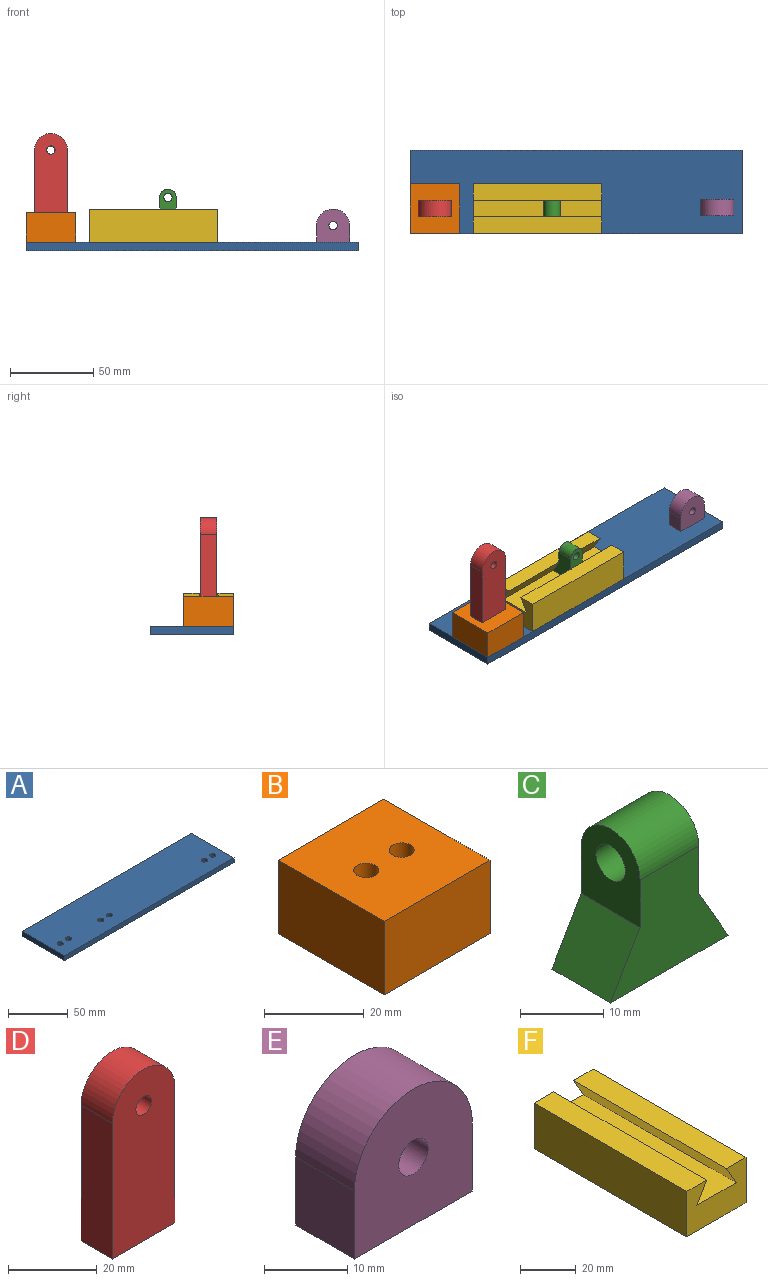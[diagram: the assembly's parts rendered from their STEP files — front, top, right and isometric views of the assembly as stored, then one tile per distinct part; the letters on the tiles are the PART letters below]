
ASSEMBLY  parts=6 mates=5
PART A: 12 faces, bbox 200x50x5 mm
  f0: plane 200x5mm, normal (0,1,0), area 1000mm2, adj f1,f9,f10,f11
  f1: plane 50x5mm, normal (-1,0,0), area 250mm2, adj f0,f2,f10,f11
  f2: plane 200x5mm, normal (0,-1,0), area 1000mm2, adj f1,f9,f10,f11
  f3: cylinder r=2.5mm len=5mm, axis (0,0,-1), area 78.5mm2, adj f10,f11
  f4: cylinder r=2.5mm len=5mm, axis (0,0,-1), area 78.5mm2, adj f10,f11
  f5: cylinder r=2.5mm len=5mm, axis (0,0,-1), area 78.5mm2, adj f10,f11
  f6: cylinder r=2.5mm len=5mm, axis (0,0,-1), area 78.5mm2, adj f10,f11
  f7: cylinder r=2.5mm len=5mm, axis (0,0,-1), area 78.5mm2, adj f10,f11
  f8: cylinder r=2.5mm len=5mm, axis (0,0,-1), area 78.5mm2, adj f10,f11
  f9: plane 50x5mm, normal (1,0,0), area 250mm2, adj f0,f2,f10,f11
  f10: plane 200x50mm, normal (0,0,1), area 9882.2mm2, adj f0,f1,f2,f3,f4,f5,f6,f7
  f11: plane 200x50mm, normal (0,0,-1), area 9882.2mm2, adj f0,f1,f2,f3,f4,f5,f6,f7
PART B: 8 faces, bbox 30x30x18 mm
  f0: plane 30x18mm, normal (0,1,0), area 540mm2, adj f1,f5,f6,f7
  f1: plane 30x18mm, normal (-1,0,0), area 540mm2, adj f0,f2,f6,f7
  f2: plane 30x18mm, normal (0,-1,0), area 540mm2, adj f1,f5,f6,f7
  f3: cylinder r=2.5mm len=18mm, axis (0,0,-1), area 282.7mm2, adj f6,f7
  f4: cylinder r=2.5mm len=18mm, axis (0,0,-1), area 282.7mm2, adj f6,f7
  f5: plane 30x18mm, normal (1,0,0), area 540mm2, adj f0,f2,f6,f7
  f6: plane 30x30mm, normal (0,0,1), area 860.7mm2, adj f0,f1,f2,f3,f4,f5
  f7: plane 30x30mm, normal (0,0,-1), area 860.7mm2, adj f0,f1,f2,f3,f4,f5
PART C: 9 faces, bbox 20x10x20.7 mm
  f0: plane 10x8.66mm, normal (-0.87,0,0.5), area 100mm2, adj f1,f3,f4,f5
  f1: plane 20x10mm, normal (0,0,-1), area 200mm2, adj f0,f2,f3,f4
  f2: plane 10x8.66mm, normal (0.87,0,0.5), area 100mm2, adj f1,f3,f4,f8
  f3: plane 20x15.66mm, normal (0,-1,0), area 199.9mm2, adj f0,f1,f2,f5,f6,f8
  f4: plane 20x15.66mm, normal (0,1,0), area 199.9mm2, adj f0,f1,f2,f5,f6,f8
  f5: plane 12x10mm, normal (-1,0,0), area 89.6mm2, adj f0,f3,f4,f6,f7
  f6: cylinder r=5mm len=10mm, axis (1,0,0), area 157.1mm2, adj f3,f4,f5,f8
  f7: cylinder r=2.5mm len=10mm, axis (1,0,0), area 157.1mm2, adj f5,f8
  f8: plane 12x10mm, normal (1,0,0), area 89.6mm2, adj f2,f3,f4,f6,f7
PART D: 11 faces, bbox 20x10x47.5 mm
  f0: plane 47.5x20mm, normal (0,1,0), area 887.4mm2, adj f1,f3,f4,f5,f6
  f1: plane 37.5x10mm, normal (-1,0,0), area 375mm2, adj f0,f2,f4,f5
  f2: plane 47.5x20mm, normal (0,-1,0), area 887.4mm2, adj f1,f3,f4,f5,f6
  f3: plane 37.5x10mm, normal (1,0,0), area 375mm2, adj f0,f2,f4,f5
  f4: plane 20x10mm, normal (0,0,-1), area 160.7mm2, adj f0,f1,f2,f3,f7,f9
  f5: cylinder r=10mm len=20mm, axis (0,-1,0), area 314.2mm2, adj f0,f1,f2,f3
  f6: cylinder r=2.5mm len=10mm, axis (0,-1,0), area 157.1mm2, adj f0,f2
  f7: cylinder r=2.5mm len=10mm, axis (0,0,-1), area 157.1mm2, adj f4,f8
  f8: plane 5x5mm, normal (0,0,-1), area 19.6mm2, adj f7
  f9: cylinder r=2.5mm len=10mm, axis (0,0,-1), area 157.1mm2, adj f4,f10
  f10: plane 5x5mm, normal (0,0,-1), area 19.6mm2, adj f9
PART E: 11 faces, bbox 20x10x20 mm
  f0: plane 10x10mm, normal (-1,0,0), area 100mm2, adj f1,f4,f5,f6
  f1: plane 20x10mm, normal (0,0,-1), area 160.7mm2, adj f0,f2,f5,f6,f7,f9
  f2: plane 10x10mm, normal (1,0,0), area 100mm2, adj f1,f4,f5,f6
  f3: cylinder r=2.5mm len=10mm, axis (0,1,0), area 157.1mm2, adj f5,f6
  f4: cylinder r=10mm len=20mm, axis (0,1,0), area 314.2mm2, adj f0,f2,f5,f6
  f5: plane 20x20mm, normal (0,-1,0), area 337.4mm2, adj f0,f1,f2,f3,f4
  f6: plane 20x20mm, normal (0,1,0), area 337.4mm2, adj f0,f1,f2,f3,f4
  f7: cylinder r=2.5mm len=5mm, axis (0,0,-1), area 78.5mm2, adj f1,f8
  f8: plane 5x5mm, normal (0,0,-1), area 19.6mm2, adj f7
  f9: cylinder r=2.5mm len=5mm, axis (0,0,-1), area 78.5mm2, adj f1,f10
  f10: plane 5x5mm, normal (0,0,-1), area 19.6mm2, adj f9
PART F: 14 faces, bbox 30x77.5x20 mm
  f0: plane 77.5x8.66mm, normal (0.87,0,-0.5), area 775mm2, adj f1,f7,f8,f9
  f1: plane 77.5x10mm, normal (0,0,1), area 775mm2, adj f0,f2,f8,f9
  f2: plane 77.5x20mm, normal (-1,0,0), area 1550mm2, adj f1,f3,f8,f9
  f3: plane 77.5x30mm, normal (0,0,-1), area 2285.7mm2, adj f2,f4,f8,f9,f10,f12
  f4: plane 77.5x20mm, normal (1,0,0), area 1550mm2, adj f3,f5,f8,f9
  f5: plane 77.5x10mm, normal (0,0,1), area 775mm2, adj f4,f6,f8,f9
  f6: plane 77.5x8.66mm, normal (-0.87,0,-0.5), area 775mm2, adj f5,f7,f8,f9
  f7: plane 77.5x20mm, normal (0,0,1), area 1550mm2, adj f0,f6,f8,f9
  f8: plane 30x20mm, normal (0,-1,0), area 470.1mm2, adj f0,f1,f2,f3,f4,f5,f6,f7
  f9: plane 30x20mm, normal (0,1,0), area 470.1mm2, adj f0,f1,f2,f3,f4,f5,f6,f7
  f10: cylinder r=2.5mm len=10mm, axis (0,0,-1), area 157.1mm2, adj f3,f11
  f11: plane 5x5mm, normal (0,0,-1), area 19.6mm2, adj f10
  f12: cylinder r=2.5mm len=10mm, axis (0,0,-1), area 157.1mm2, adj f3,f13
  f13: plane 5x5mm, normal (0,0,-1), area 19.6mm2, adj f12
PLACE A t=(61.36,-48.17,28.82)mm
PLACE B t=(66.44,-6.03,33.82)mm
PLACE C rot(axis=(0,0,-1),90deg) t=(-98.16,-221.76,83.2)mm
PLACE D t=(27.27,-1.24,51.82)mm
PLACE E t=(276.42,-25.77,33.82)mm
PLACE F rot(axis=(0,0,-1),90deg) t=(-73.14,-215.25,112.62)mm
MATE fastened F.f12 <-> A.f5  axis (0,0,-1) through (-130.64,-31.4,33.82)mm
MATE fastened B.f3 <-> A.f3  axis (0,0,-1) through (-178.64,-31.4,33.82)mm
MATE fastened D.f7 <-> B.f4  axis (0,0,-1) through (-168.64,-31.4,51.82)mm
MATE planar C.f1 <-> F.f7  axis (0,0,-1) through (-103.16,-31.4,45.16)mm
MATE fastened E.f7 <-> A.f8  axis (0,0,-1) through (1.36,-31.4,33.82)mm
